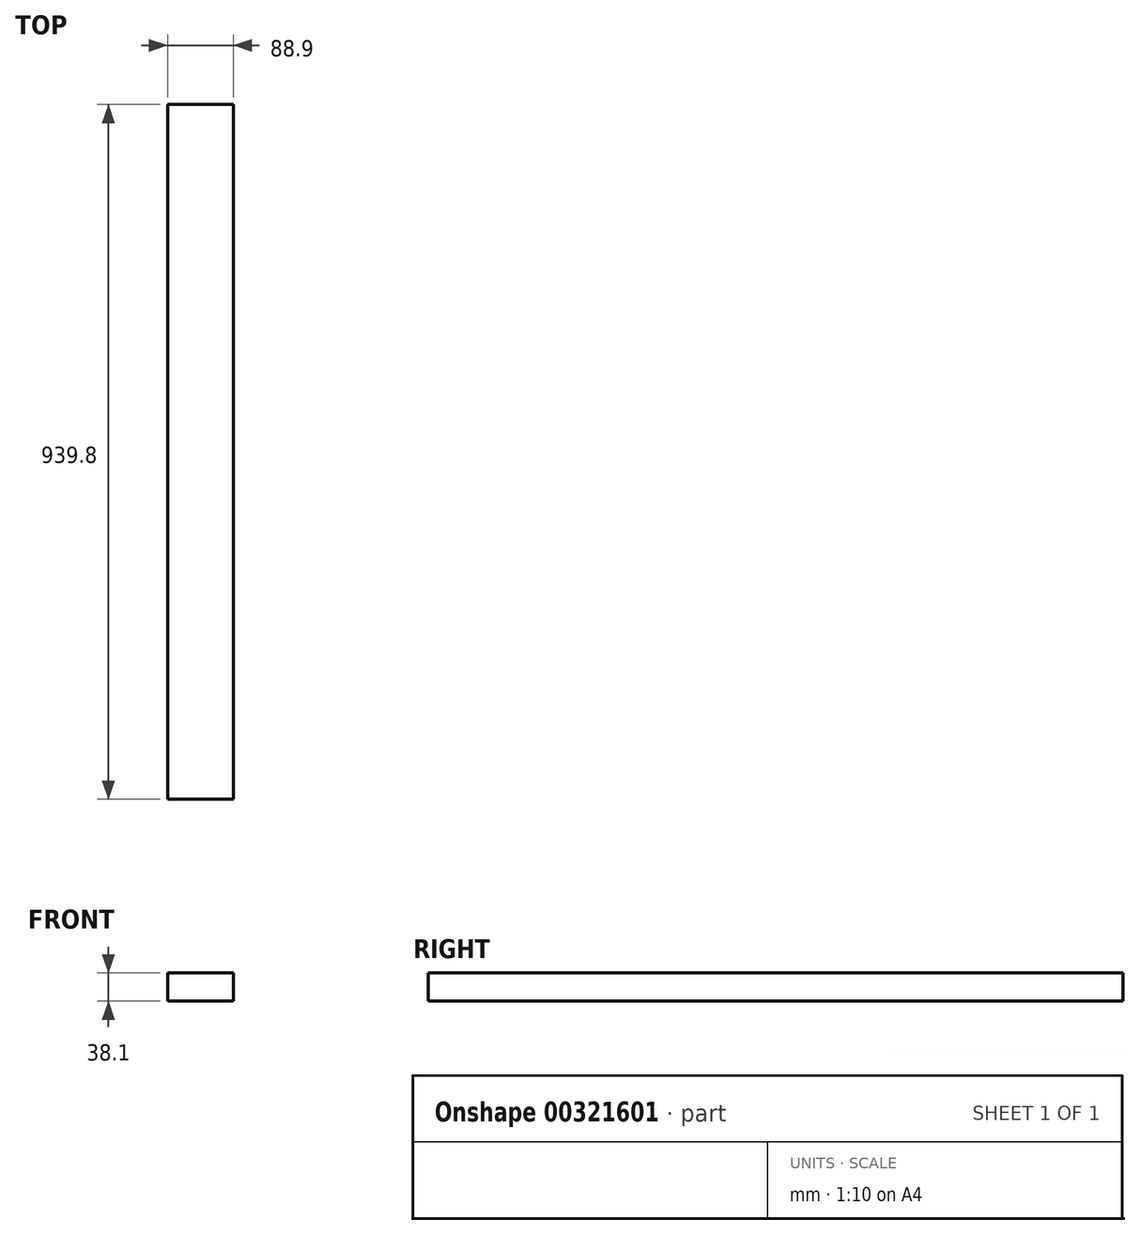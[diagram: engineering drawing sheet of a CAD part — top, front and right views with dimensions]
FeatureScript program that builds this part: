
annotation { "Feature Type Name" : "Feature", "Feature Type Description" : "" }
export const myFeature = defineFeature(function(context is Context, id is Id, definition is map)
    precondition{}
    {
        {
            var Q0;
            Q0=qCreatedBy(makeId("Front.planeOp"),FACE);
            var sketch = newSketch(context, id + "F0", { "sketchPlane" : qUnion([Q0])});
            skLineSegment(sketch, "E0.bottom", {"start": v(-44.45, 19.05) * mm, "end": v(44.45, 19.05) * mm});
            skLineSegment(sketch, "E0.top", {"start": v(-44.45, -19.05) * mm, "end": v(44.45, -19.05) * mm});
            skLineSegment(sketch, "E0.left", {"start": v(-44.45, 19.05) * mm, "end": v(-44.45, -19.05) * mm});
            skLineSegment(sketch, "E0.right", {"start": v(44.45, 19.05) * mm, "end": v(44.45, -19.05) * mm});
            skSolve(sketch);
        }
        {
            var Q0;
            Q0=makeQuery(id+"F0.imprint","IMPRINT",FACE,{"disambiguationData":[TD([[makeQuery(id+"F0.imprint","IMPRINT",EDGE,{"derivedFrom":sQuery(id+"F0.wireOp",EDGE,"E0.bottom")}),-1.0]])]});
            extrude(context, id + "F1", {"entities" : qUnion([Q0]), "depth" : 939.8 * mm});
        }
    });
